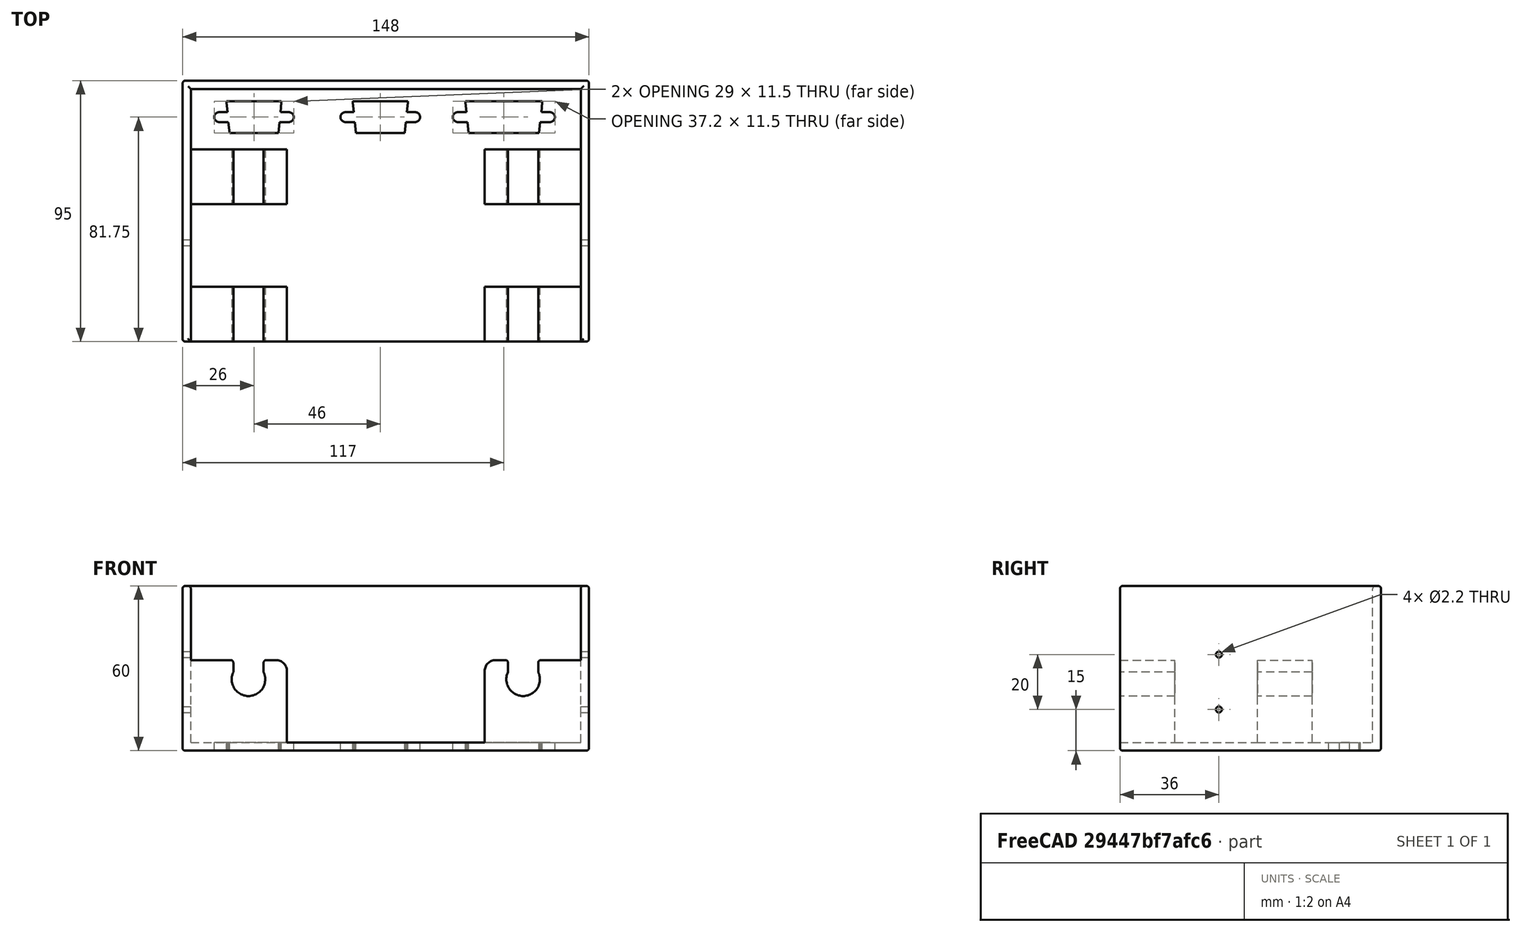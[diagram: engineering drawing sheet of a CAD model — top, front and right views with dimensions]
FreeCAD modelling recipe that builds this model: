
FCSTD DOCUMENT  (FreeCAD 0.18R16146 (Git))
Label: AbdeckungUndStecker
License: All rights reserved
LicenseURL: http://en.wikipedia.org/wiki/All_rights_reserved
objects: Part::Box×14, Part::Cut×10, Part::Cylinder×10, Part::MultiFuse×4, Part::Fillet×3, Part::Chamfer×3
note: 44 computed .brp shape members not serialized (recipe doc carries the construction recipe); baked Part::Feature solids carry a one-line shape summary decoded from their .brp

FEATURE [Part::Box] Box  label="Cube"
  AttacherType = Attacher::AttachEngine3D
  Height = 60
  Length = 148
  Width = 95
FEATURE [Part::Box] Box001  label="Cube001"
  AttacherType = Attacher::AttachEngine3D
  Height = 60
  Length = 142
  Placement = pos=(3,0,3) rot=(0,0,1;0rad)
  Width = 92
FEATURE [Part::Cut] Cut
  Base = -> Box
  Tool = -> Box001
FEATURE [Part::Cylinder] Cylinder
  Angle = 360
  AttacherType = Attacher::AttachEngine3D
  Height = 80
  Placement = pos=(24,73,26) rot=(1,0,0;1.5708rad)
  Radius = 6.1
FEATURE [Part::Cylinder] Cylinder001
  Angle = 360
  AttacherType = Attacher::AttachEngine3D
  Height = 80
  Placement = pos=(124,73,26) rot=(1,0,0;1.5708rad)
  Radius = 6.1
FEATURE [Part::Box] Box002  label="Cube002"
  AttacherType = Attacher::AttachEngine3D
  Height = 30
  Length = 35
  Placement = pos=(3,0,3) rot=(0,0,1;0rad)
  Width = 20
FEATURE [Part::Box] Box003  label="Cube003"
  AttacherType = Attacher::AttachEngine3D
  Height = 30
  Length = 35
  Placement = pos=(3,50,3) rot=(0,0,1;0rad)
  Width = 20
FEATURE [Part::Box] Box004  label="Cube004"
  AttacherType = Attacher::AttachEngine3D
  Height = 30
  Length = 35
  Placement = pos=(110,0,3) rot=(0,0,1;0rad)
  Width = 20
FEATURE [Part::Box] Box005  label="Cube005"
  AttacherType = Attacher::AttachEngine3D
  Height = 30
  Length = 35
  Placement = pos=(110,50,3) rot=(0,0,1;0rad)
  Width = 20
FEATURE [Part::Box] Box006  label="Cube006"
  AttacherType = Attacher::AttachEngine3D
  Height = 15
  Length = 11
  Placement = pos=(118.5,0,27) rot=(0,0,1;0rad)
  Width = 73
FEATURE [Part::Box] Box007  label="Cube007"
  AttacherType = Attacher::AttachEngine3D
  Height = 15
  Length = 11
  Placement = pos=(18.5,0,27) rot=(0,0,1;0rad)
  Width = 73
FEATURE [Part::MultiFuse] Fusion
  Shapes = -> [Cut,Box002,Box003,Box004,Box005]
FEATURE [Part::Cut] Cut001
  Base = -> Fusion
  Tool = -> Cylinder
FEATURE [Part::Cut] Cut002
  Base = -> Cut001
  Tool = -> Cylinder001
FEATURE [Part::Cut] Cut003
  Base = -> Cut002
  Tool = -> Box007
FEATURE [Part::Cut] Cut004
  Base = -> Cut003
  Tool = -> Box006
FEATURE [Part::Fillet] Fillet
  Base = -> Cut004
  Edges = 8 edges r=1: [Edge14,Edge48,Edge116,Edge117,Edge121,Edge122,Edge126,Edge130]
FEATURE [Part::Fillet] Fillet001
  Base = -> Fillet
  Edges = 4 edges r=4: [Edge14,Edge95,Edge115,Edge133]
FEATURE [Part::Box] Box008  label="Cube008"
  AttacherType = Attacher::AttachEngine3D
  Height = 10
  Length = 28
  Width = 11.5
FEATURE [Part::Chamfer] Chamfer
  Base = -> Box008
  Edges = 2 edges: [Edge1 r1=11 r2=1.2,Edge5 r1=11 r2=1.2]
FEATURE [Part::Cylinder] Cylinder002
  Angle = 360
  AttacherType = Attacher::AttachEngine3D
  Height = 10
  Placement = pos=(-2.8,5.75,0) rot=(0,0,1;0rad)
  Radius = 1.8
FEATURE [Part::Cylinder] Cylinder003
  Angle = 360
  AttacherType = Attacher::AttachEngine3D
  Height = 10
  Placement = pos=(30.8,5.75,0) rot=(0,0,1;0rad)
  Radius = 1.8
FEATURE [Part::Box] Box009  label="Cube009"
  AttacherType = Attacher::AttachEngine3D
  Height = 10
  Length = 33.6
  Placement = pos=(-2.8,3.95,0) rot=(0,0,1;0rad)
  Width = 3.6
FEATURE [Part::MultiFuse] Fusion001  label="SteckerLang"
  Placement = pos=(103,76,0) rot=(0,0,1;0rad)
  Shapes = -> [Chamfer,Cylinder003,Box009,Cylinder002]
FEATURE [Part::Box] Box010  label="Cube010"
  AttacherType = Attacher::AttachEngine3D
  Height = 10
  Length = 20
  Width = 11.5
FEATURE [Part::Chamfer] Chamfer001
  Base = -> Box010
  Edges = 2 edges: [Edge1 r1=11 r2=1.1,Edge5 r1=11 r2=1.1]
FEATURE [Part::Cylinder] Cylinder004
  Angle = 360
  AttacherType = Attacher::AttachEngine3D
  Height = 10
  Placement = pos=(-2.7,5.75,0) rot=(0,0,1;0rad)
  Radius = 1.8
FEATURE [Part::Cylinder] Cylinder005
  Angle = 360
  AttacherType = Attacher::AttachEngine3D
  Height = 10
  Placement = pos=(22.7,5.75,0) rot=(0,0,1;0rad)
  Radius = 1.8
FEATURE [Part::Box] Box011  label="Cube011"
  AttacherType = Attacher::AttachEngine3D
  Height = 10
  Length = 25.4
  Placement = pos=(-2.7,3.95,0) rot=(0,0,1;0rad)
  Width = 3.6
FEATURE [Part::MultiFuse] Fusion002  label="SteckerKurz"
  Placement = pos=(16,76,0) rot=(0,0,1;0rad)
  Shapes = -> [Chamfer001,Box011,Cylinder005,Cylinder004]
FEATURE [Part::Cylinder] Cylinder006
  Angle = 360
  AttacherType = Attacher::AttachEngine3D
  Height = 10
  Placement = pos=(22.7,5.75,0) rot=(0,0,1;0rad)
  Radius = 1.8
FEATURE [Part::Box] Box012  label="Cube012"
  AttacherType = Attacher::AttachEngine3D
  Height = 10
  Length = 20
  Width = 11.5
FEATURE [Part::Cylinder] Cylinder007
  Angle = 360
  AttacherType = Attacher::AttachEngine3D
  Height = 10
  Placement = pos=(-2.7,5.75,0) rot=(0,0,1;0rad)
  Radius = 1.8
FEATURE [Part::Box] Box013  label="Cube013"
  AttacherType = Attacher::AttachEngine3D
  Height = 10
  Length = 25.4
  Placement = pos=(-2.7,3.95,0) rot=(0,0,1;0rad)
  Width = 3.6
FEATURE [Part::Chamfer] Chamfer002
  Base = -> Box012
  Edges = 2 edges: [Edge1 r1=11 r2=1.1,Edge5 r1=11 r2=1.1]
FEATURE [Part::MultiFuse] Fusion003  label="SteckerKurz001"
  Placement = pos=(62,76,0) rot=(0,0,1;0rad)
  Shapes = -> [Chamfer002,Box013,Cylinder006,Cylinder007]
FEATURE [Part::Cut] Cut005
  Base = -> Fillet001
  Tool = -> Fusion001
FEATURE [Part::Cut] Cut006
  Base = -> Cut005
  Tool = -> Fusion003
FEATURE [Part::Cut] Cut007
  Base = -> Cut006
  Tool = -> Fusion002
FEATURE [Part::Cylinder] Cylinder008
  Angle = 360
  AttacherType = Attacher::AttachEngine3D
  Height = 150
  Placement = pos=(-1,36,15) rot=(0,1,0;1.5708rad)
  Radius = 1.1
FEATURE [Part::Cylinder] Cylinder009
  Angle = 360
  AttacherType = Attacher::AttachEngine3D
  Height = 150
  Placement = pos=(-1,36,35) rot=(0,1,0;1.5708rad)
  Radius = 1.1
FEATURE [Part::Cut] Cut008
  Base = -> Cut007
  Tool = -> Cylinder008
FEATURE [Part::Cut] Cut009
  Base = -> Cut008
  Tool = -> Cylinder009
FEATURE [Part::Fillet] Fillet002
  Base = -> Cut009
  Edges = 16 edges r=1: [Edge24,Edge25,Edge31,Edge32,Edge33,Edge104,Edge105,Edge106,Edge109,Edge110,Edge111,Edge112,Edge113,Edge138,Edge139,Edge142]
